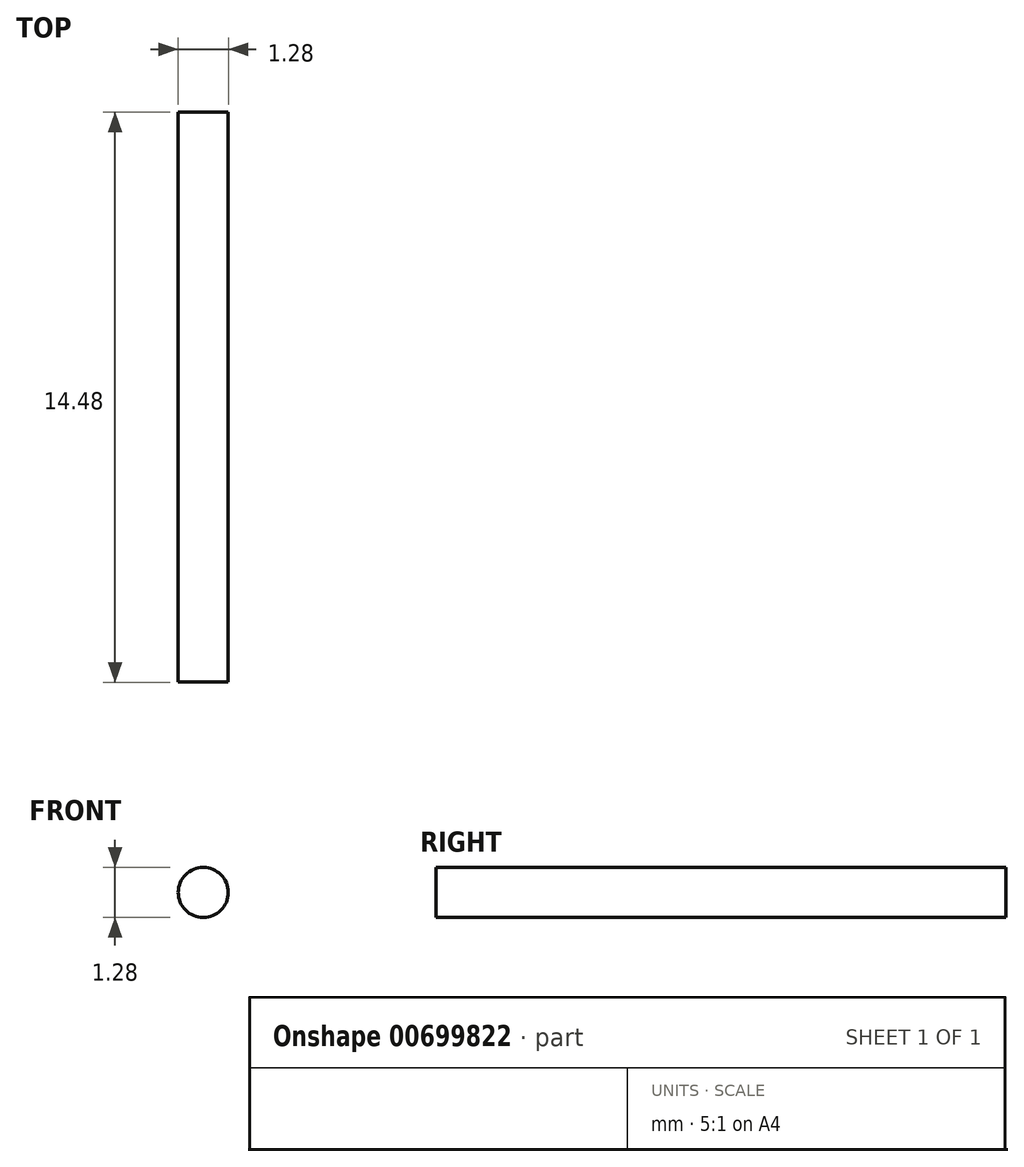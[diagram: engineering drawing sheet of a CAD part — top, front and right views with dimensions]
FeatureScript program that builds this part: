
annotation { "Feature Type Name" : "Feature", "Feature Type Description" : "" }
export const myFeature = defineFeature(function(context is Context, id is Id, definition is map)
    precondition{}
    {
        {
            var Q0;
            Q0=qCreatedBy(makeId("Front.planeOp"),FACE);
            var sketch = newSketch(context, id + "F0", { "sketchPlane" : qUnion([Q0])});
            skCircle(sketch, "E0", {"center": v(0, 0) * mm, "radius": 0.64 * mm});
            skSolve(sketch);
        }
        {
            var Q0;
            Q0=qSketchRegion(id+"F0",true);
            extrude(context, id + "F1", {"entities" : qUnion([Q0]), "depth" : 14.48 * mm});
        }
    });
